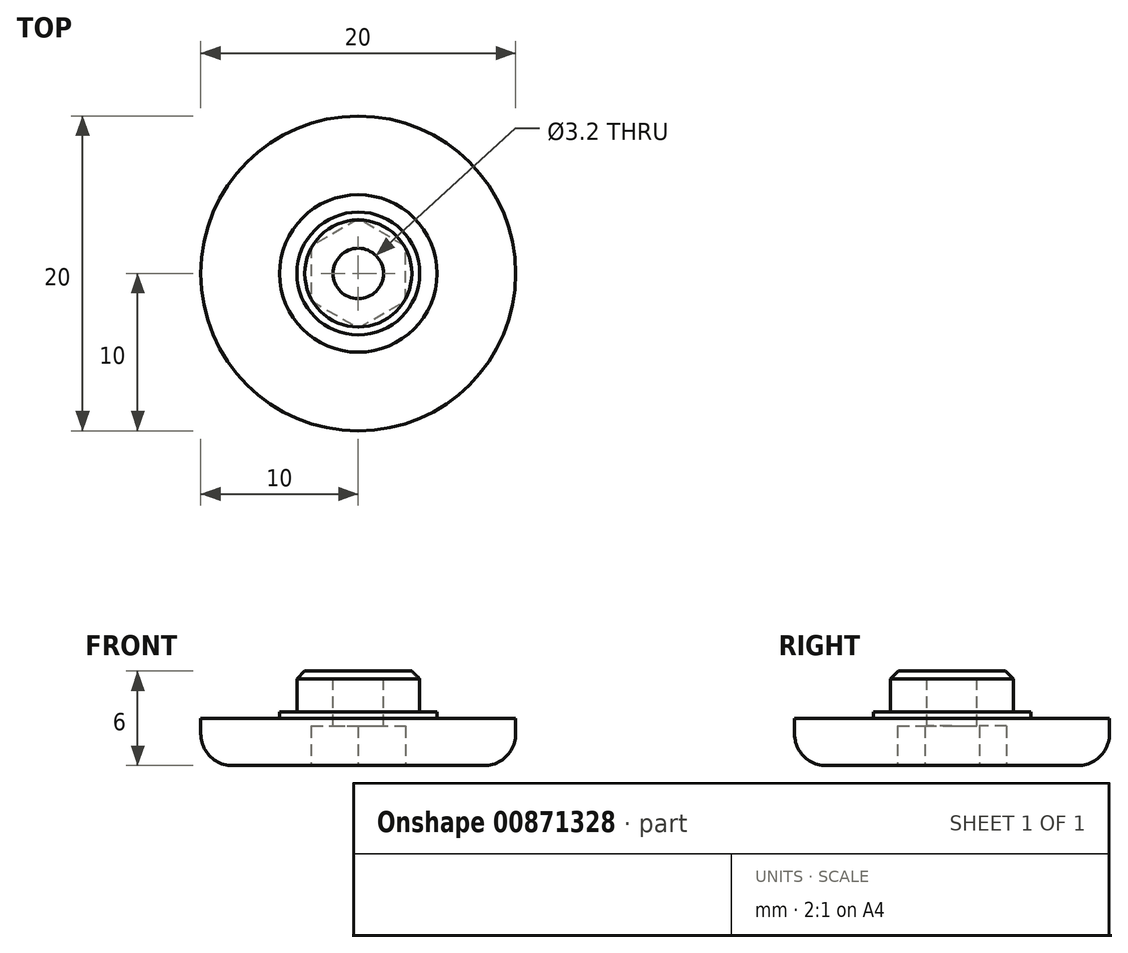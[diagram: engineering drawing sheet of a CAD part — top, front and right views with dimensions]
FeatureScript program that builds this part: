
annotation { "Feature Type Name" : "Feature", "Feature Type Description" : "" }
export const myFeature = defineFeature(function(context is Context, id is Id, definition is map)
    precondition{}
    {
        {
            var Q0;
            Q0=qCreatedBy(makeId("Front.planeOp"),FACE);
            var sketch = newSketch(context, id + "F0", { "sketchPlane" : qUnion([Q0])});
            skLineSegment(sketch, "E0", {"start": v(0, 6) * mm, "end": v(3.9, 6) * mm});
            skLineSegment(sketch, "E1", {"start": v(3.9, 6) * mm, "end": v(3.9, 3) * mm});
            skLineSegment(sketch, "E2", {"start": v(3.9, 3) * mm, "end": v(10, 3) * mm});
            skLineSegment(sketch, "E3", {"start": v(10, 3) * mm, "end": v(10, 0) * mm});
            skLineSegment(sketch, "E4", {"start": v(10, 0) * mm, "end": v(0, 0) * mm});
            skLineSegment(sketch, "E5", {"start": v(0, 6) * mm, "end": v(0, 0) * mm});
            skSolve(sketch);
        }
        {
            var Q0;
            Q0=makeQuery(id+"F0.imprint","IMPRINT",FACE,{"disambiguationData":[TD([[makeQuery(id+"F0.imprint","IMPRINT",EDGE,{"derivedFrom":sQuery(id+"F0.wireOp",EDGE,"E0")}),-1.0]])]});
            var Q1;
            Q1=sQuery(id+"F0.wireOp",EDGE,"E5");
            revolve(context, id + "F1", {"surfaceOperationType" : NewSurfaceOperationType.NEW, "entities" : qUnion([Q0]), "axis" : qUnion([Q1]), "revolveType" : RevolveType.FULL});
        }
        {
            var Q0;
            Q0=makeQuery(id+"F1.opRevolve","SWEPT_EDGE",EDGE,{"disambiguationData":[OSD([sQuery(id+"F0.wireOp",EDGE,"E0"),sQuery(id+"F0.wireOp",EDGE,"E1")])]});
            chamfer(context, id + "F2", {"entities" : qUnion([Q0]), "width" : 0.5 * mm, "tangentPropagation" : true});
        }
        {
            var Q0;
            Q0=makeQuery(id+"F1.opRevolve","SWEPT_FACE",FACE,{"disambiguationData":[OSD([sQuery(id+"F0.wireOp",EDGE,"E2")])]});
            var sketch = newSketch(context, id + "F3", { "sketchPlane" : qUnion([Q0])});
            skCircle(sketch, "E6", {"center": v(0, 0) * mm, "radius": 5 * mm});
            skSolve(sketch);
        }
        {
            var Q0;
            Q0=makeQuery(id+"F3.imprint","IMPRINT",FACE,{"disambiguationData":[TD([[makeQuery(id+"F3.imprint","IMPRINT",EDGE,{"derivedFrom":sQuery(id+"F3.wireOp",EDGE,"E6")}),1.0]])]});
            extrude(context, id + "F4", {"entities" : qUnion([Q0]), "operationType" : NewBodyOperationType.ADD, "depth" : 0.4 * mm, "offsetDistance" : 25 * mm});
        }
        {
            var Q0;
            Q0=makeQuery(id+"F1.opRevolve","SWEPT_EDGE",EDGE,{"disambiguationData":[OSD([sQuery(id+"F0.wireOp",EDGE,"E3"),sQuery(id+"F0.wireOp",EDGE,"E4")])]});
            fillet(context, id + "F5", {"entities" : qUnion([Q0]), "radius" : 2 * mm, "tangentPropagation" : true, "allowEdgeOverflow" : false});
        }
        {
            var Q0;
            Q0=makeQuery(id+"F1.opRevolve","SWEPT_FACE",FACE,{"disambiguationData":[OSD([sQuery(id+"F0.wireOp",EDGE,"E0")])]});
            var sketch = newSketch(context, id + "F6", { "sketchPlane" : qUnion([Q0])});
            skCircle(sketch, "E7", {"center": v(0, 0) * mm, "radius": 1.6 * mm});
            skSolve(sketch);
        }
        {
            var Q0;
            Q0=makeQuery(id+"F6.imprint","IMPRINT",FACE,{"disambiguationData":[TD([[makeQuery(id+"F6.imprint","IMPRINT",EDGE,{"derivedFrom":sQuery(id+"F6.wireOp",EDGE,"E7")}),1.0]])]});
            extrude(context, id + "F7", {"entities" : qUnion([Q0]), "operationType" : NewBodyOperationType.REMOVE, "oppositeDirection" : true, "depth" : 25 * mm, "offsetDistance" : 25 * mm});
        }
        {
            var Q0;
            Q0=makeQuery(id+"F1.opRevolve","SWEPT_FACE",FACE,{"disambiguationData":[OSD([sQuery(id+"F0.wireOp",EDGE,"E4")])]});
            var sketch = newSketch(context, id + "F8", { "sketchPlane" : qUnion([Q0])});
            skCircle(sketch, "E8.cCircle", {"center": v(0, 0) * mm, "radius": 3 * mm, "construction": true});
            skLineSegment(sketch, "E8.0", {"start": v(3, 1.73) * mm, "end": v(3, -1.73) * mm});
            skLineSegment(sketch, "E8.1", {"start": v(3, -1.73) * mm, "end": v(0, -3.46) * mm});
            skLineSegment(sketch, "E8.2", {"start": v(0, -3.46) * mm, "end": v(-3, -1.73) * mm});
            skLineSegment(sketch, "E8.3", {"start": v(-3, -1.73) * mm, "end": v(-3, 1.73) * mm});
            skLineSegment(sketch, "E8.4", {"start": v(-3, 1.73) * mm, "end": v(0, 3.46) * mm});
            skLineSegment(sketch, "E8.5", {"start": v(0, 3.46) * mm, "end": v(3, 1.73) * mm});
            skPoint(sketch, "E8.0.midPoint", {"position": v(3, 0) * mm});
            skSolve(sketch);
        }
        {
            var Q0;
            Q0=makeQuery(id+"F8.imprint","IMPRINT",FACE,{"disambiguationData":[TD([[makeQuery(id+"F8.imprint","IMPRINT",EDGE,{"derivedFrom":sQuery(id+"F8.wireOp",EDGE,"E8.0")}),-1.0]])]});
            extrude(context, id + "F9", {"entities" : qUnion([Q0]), "operationType" : NewBodyOperationType.REMOVE, "oppositeDirection" : true, "depth" : 2.5 * mm, "offsetDistance" : 25 * mm});
        }
    });
